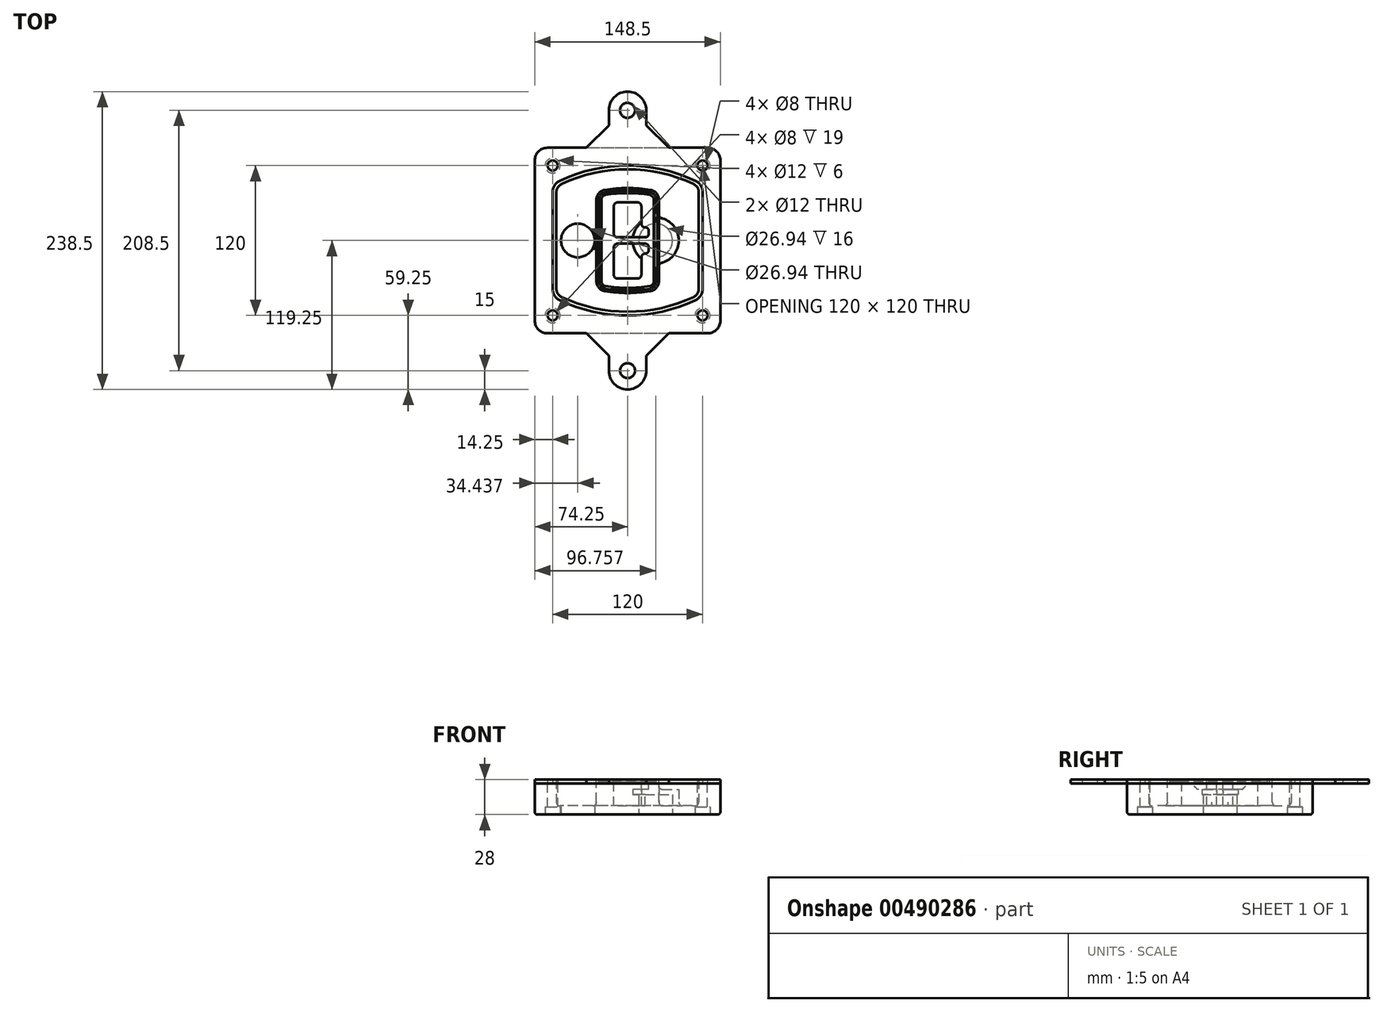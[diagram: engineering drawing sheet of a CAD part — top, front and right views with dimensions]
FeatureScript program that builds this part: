
annotation { "Feature Type Name" : "Feature", "Feature Type Description" : "" }
export const myFeature = defineFeature(function(context is Context, id is Id, definition is map)
    precondition{}
    {
        {
            var Q0;
            Q0=qCreatedBy(makeId("Top.planeOp"),FACE);
            var sketch = newSketch(context, id + "F0", { "sketchPlane" : qUnion([Q0])});
            skPoint(sketch, "E0.rect.middle", {"position": v(0, 0) * mm});
            skLineSegment(sketch, "E1.bottom", {"start": v(-64.25, -74.25) * mm, "end": v(64.25, -74.25) * mm});
            skLineSegment(sketch, "E1.top", {"start": v(-64.25, 74.25) * mm, "end": v(64.25, 74.25) * mm});
            skLineSegment(sketch, "E1.left", {"start": v(-74.25, -64.25) * mm, "end": v(-74.25, 64.25) * mm});
            skLineSegment(sketch, "E1.right", {"start": v(74.25, -64.25) * mm, "end": v(74.25, 64.25) * mm});
            skLineSegment(sketch, "E2", {"start": v(-74.25, 74.25) * mm, "end": v(74.25, -74.25) * mm, "construction": true});
            skLineSegment(sketch, "E3", {"start": v(74.25, 74.25) * mm, "end": v(-74.25, -74.25) * mm, "construction": true});
            skCircle(sketch, "E4", {"center": v(-60, 60) * mm, "radius": 4 * mm});
            skCircle(sketch, "E5", {"center": v(60, 60) * mm, "radius": 4 * mm});
            skCircle(sketch, "E6", {"center": v(60, -60) * mm, "radius": 4 * mm});
            skCircle(sketch, "E7", {"center": v(-60, -60) * mm, "radius": 4 * mm});
            skLineSegment(sketch, "E8", {"start": v(-60, 60) * mm, "end": v(60, 60) * mm, "construction": true});
            skLineSegment(sketch, "E9", {"start": v(60, 60) * mm, "end": v(60, -60) * mm, "construction": true});
            skLineSegment(sketch, "E10", {"start": v(60, -60) * mm, "end": v(-60, -60) * mm, "construction": true});
            skLineSegment(sketch, "E11", {"start": v(-60, -60) * mm, "end": v(-60, 60) * mm, "construction": true});
            skLineSegment(sketch, "E12", {"start": v(-60, 38.83) * mm, "end": v(-60, -38.83) * mm});
            skLineSegment(sketch, "E13", {"start": v(60, 38.83) * mm, "end": v(60, -38.83) * mm});
            skArc(sketch, "E14", {"start": v(54.26, 47.88) * mm, "mid": v(0, 60) * mm, "end": v(-54.26, 47.88) * mm});
            skArc(sketch, "E15", {"start": v(-54.26, -47.88) * mm, "mid": v(0, -60) * mm, "end": v(54.26, -47.88) * mm});
            skLineSegment(sketch, "E16", {"start": v(-60, 0) * mm, "end": v(60, 0) * mm, "construction": true});
            skPoint(sketch, "E17.visualSharp", {"position": v(-60, -45) * mm});
            skArc(sketch, "E17.filletArc", {"start": v(-60, -38.83) * mm, "mid": v(-58.44, -44.2) * mm, "end": v(-54.26, -47.88) * mm});
            skPoint(sketch, "E18.visualSharp", {"position": v(-60, 45) * mm});
            skArc(sketch, "E18.filletArc", {"start": v(-54.26, 47.88) * mm, "mid": v(-58.44, 44.2) * mm, "end": v(-60, 38.83) * mm});
            skPoint(sketch, "E19.visualSharp", {"position": v(60, 45) * mm});
            skArc(sketch, "E19.filletArc", {"start": v(60, 38.83) * mm, "mid": v(58.44, 44.2) * mm, "end": v(54.26, 47.88) * mm});
            skPoint(sketch, "E20.visualSharp", {"position": v(60, -45) * mm});
            skArc(sketch, "E20.filletArc", {"start": v(54.26, -47.88) * mm, "mid": v(58.44, -44.2) * mm, "end": v(60, -38.83) * mm});
            skPoint(sketch, "E21.visualSharp", {"position": v(-74.25, 74.25) * mm});
            skArc(sketch, "E21.filletArc", {"start": v(-64.25, 74.25) * mm, "mid": v(-71.32, 71.32) * mm, "end": v(-74.25, 64.25) * mm});
            skPoint(sketch, "E22.visualSharp", {"position": v(74.25, 74.25) * mm});
            skArc(sketch, "E22.filletArc", {"start": v(74.25, 64.25) * mm, "mid": v(71.32, 71.32) * mm, "end": v(64.25, 74.25) * mm});
            skPoint(sketch, "E23.visualSharp", {"position": v(74.25, -74.25) * mm});
            skArc(sketch, "E23.filletArc", {"start": v(64.25, -74.25) * mm, "mid": v(71.32, -71.32) * mm, "end": v(74.25, -64.25) * mm});
            skPoint(sketch, "E24.visualSharp", {"position": v(-74.25, -74.25) * mm});
            skArc(sketch, "E24.filletArc", {"start": v(-74.25, -64.25) * mm, "mid": v(-71.32, -71.32) * mm, "end": v(-64.25, -74.25) * mm});
            skArc(sketch, "E25.0", {"start": v(57, 38.83) * mm, "mid": v(55.9, 42.58) * mm, "end": v(52.98, 45.17) * mm});
            skLineSegment(sketch, "E25.1", {"start": v(57, 38.83) * mm, "end": v(57, -38.83) * mm});
            skArc(sketch, "E25.2", {"start": v(52.98, -45.17) * mm, "mid": v(55.9, -42.58) * mm, "end": v(57, -38.83) * mm});
            skArc(sketch, "E25.3", {"start": v(-52.98, -45.17) * mm, "mid": v(0, -57) * mm, "end": v(52.98, -45.17) * mm});
            skArc(sketch, "E25.4", {"start": v(-57, -38.83) * mm, "mid": v(-55.9, -42.58) * mm, "end": v(-52.98, -45.17) * mm});
            skArc(sketch, "E25.5", {"start": v(52.98, 45.17) * mm, "mid": v(0, 57) * mm, "end": v(-52.98, 45.17) * mm});
            skLineSegment(sketch, "E25.6", {"start": v(-57, 38.83) * mm, "end": v(-57, -38.83) * mm});
            skArc(sketch, "E25.7", {"start": v(-52.98, 45.17) * mm, "mid": v(-55.9, 42.58) * mm, "end": v(-57, 38.83) * mm});
            skArc(sketch, "E26.0", {"start": v(-55.96, 51.5) * mm, "mid": v(-61.82, 46.33) * mm, "end": v(-64, 38.83) * mm});
            skArc(sketch, "E26.1", {"start": v(55.96, 51.5) * mm, "mid": v(0, 64) * mm, "end": v(-55.96, 51.5) * mm});
            skArc(sketch, "E26.2", {"start": v(64, 38.83) * mm, "mid": v(61.82, 46.33) * mm, "end": v(55.96, 51.5) * mm});
            skLineSegment(sketch, "E26.3", {"start": v(64, 38.83) * mm, "end": v(64, -38.83) * mm});
            skArc(sketch, "E26.4", {"start": v(55.96, -51.5) * mm, "mid": v(61.82, -46.33) * mm, "end": v(64, -38.83) * mm});
            skLineSegment(sketch, "E26.5", {"start": v(-64, 38.83) * mm, "end": v(-64, -38.83) * mm});
            skArc(sketch, "E26.6", {"start": v(-55.96, -51.5) * mm, "mid": v(0, -64) * mm, "end": v(55.96, -51.5) * mm});
            skArc(sketch, "E26.7", {"start": v(-64, -38.83) * mm, "mid": v(-61.82, -46.33) * mm, "end": v(-55.96, -51.5) * mm});
            skSolve(sketch);
        }
        {
            var Q0;
            Q0=makeQuery(id+"F0.imprint","IMPRINT",FACE,{"disambiguationData":[TD([[makeQuery(id+"F0.imprint","IMPRINT",EDGE,{"derivedFrom":sQuery(id+"F0.wireOp",EDGE,"E1.bottom")}),1.0]])]});
            var Q1;
            Q1=makeQuery(id+"F0.imprint","IMPRINT",FACE,{"disambiguationData":[TD([[makeQuery(id+"F0.imprint","IMPRINT",EDGE,{"derivedFrom":sQuery(id+"F0.wireOp",EDGE,"E12")}),1.0]])]});
            var Q2;
            Q2=makeQuery(id+"F0.imprint","IMPRINT",FACE,{"disambiguationData":[TD([[makeQuery(id+"F0.imprint","IMPRINT",EDGE,{"derivedFrom":sQuery(id+"F0.wireOp",EDGE,"E25.0")}),1.0]])]});
            var Q3;
            Q3=makeQuery(id+"F0.imprint","IMPRINT",FACE,{"disambiguationData":[TD([[makeQuery(id+"F0.imprint","IMPRINT",EDGE,{"derivedFrom":sQuery(id+"F0.wireOp",EDGE,"E12")}),-1.0]])]});
            extrude(context, id + "F1", {"entities" : qUnion([Q0, Q1, Q2, Q3]), "oppositeDirection" : true, "depth" : 25 * mm});
        }
        {
            var Q0;
            Q0=makeQuery(id+"F0.imprint","IMPRINT",FACE,{"disambiguationData":[TD([[makeQuery(id+"F0.imprint","IMPRINT",EDGE,{"derivedFrom":sQuery(id+"F0.wireOp",EDGE,"E12")}),1.0]])]});
            extrude(context, id + "F2", {"entities" : qUnion([Q0]), "operationType" : NewBodyOperationType.ADD, "depth" : 3 * mm});
        }
        {
            var Q0;
            Q0=makeQuery(id+"F0.imprint","IMPRINT",FACE,{"disambiguationData":[TD([[makeQuery(id+"F0.imprint","IMPRINT",EDGE,{"derivedFrom":sQuery(id+"F0.wireOp",EDGE,"E25.0")}),1.0]])]});
            extrude(context, id + "F3", {"entities" : qUnion([Q0]), "operationType" : NewBodyOperationType.REMOVE, "oppositeDirection" : true, "depth" : 18 * mm});
        }
        {
            var Q0;
            Q0=makeQuery(id+"F2.opExtrude","CAP_FACE",FACE,{"disambiguationData":[OSD([sQuery(id+"F0.wireOp",EDGE,"E12"),sQuery(id+"F0.wireOp",EDGE,"E13"),sQuery(id+"F0.wireOp",EDGE,"E14"),sQuery(id+"F0.wireOp",EDGE,"E15"),sQuery(id+"F0.wireOp",EDGE,"E17.filletArc"),sQuery(id+"F0.wireOp",EDGE,"E18.filletArc"),sQuery(id+"F0.wireOp",EDGE,"E19.filletArc"),sQuery(id+"F0.wireOp",EDGE,"E20.filletArc"),sQuery(id+"F0.wireOp",EDGE,"E25.0"),sQuery(id+"F0.wireOp",EDGE,"E25.1"),sQuery(id+"F0.wireOp",EDGE,"E25.2"),sQuery(id+"F0.wireOp",EDGE,"E25.3"),sQuery(id+"F0.wireOp",EDGE,"E25.4"),sQuery(id+"F0.wireOp",EDGE,"E25.5"),sQuery(id+"F0.wireOp",EDGE,"E25.6"),sQuery(id+"F0.wireOp",EDGE,"E25.7")])],"isStart":false});
            var sketch = newSketch(context, id + "F4", { "sketchPlane" : qUnion([Q0])});
            skArc(sketch, "E27.0", {"start": v(-18.34, -40.45) * mm, "mid": v(0, -42) * mm, "end": v(18.34, -40.45) * mm});
            skArc(sketch, "E28.0", {"start": v(18.34, 40.45) * mm, "mid": v(0, 42) * mm, "end": v(-18.34, 40.45) * mm});
            skLineSegment(sketch, "E29", {"start": v(-25, 32.57) * mm, "end": v(-25, -32.57) * mm});
            skLineSegment(sketch, "E30", {"start": v(25, 32.57) * mm, "end": v(25, -32.57) * mm});
            skLineSegment(sketch, "E31", {"start": v(-25, 39.1) * mm, "end": v(25, 39.1) * mm, "construction": true});
            skLineSegment(sketch, "E32", {"start": v(-25, -39.1) * mm, "end": v(25, -39.1) * mm, "construction": true});
            skPoint(sketch, "E33.visualSharp", {"position": v(-25, 39.1) * mm});
            skArc(sketch, "E33.filletArc", {"start": v(-18.34, 40.45) * mm, "mid": v(-23.11, 37.73) * mm, "end": v(-25, 32.57) * mm});
            skPoint(sketch, "E34.visualSharp", {"position": v(25, 39.1) * mm});
            skArc(sketch, "E34.filletArc", {"start": v(25, 32.57) * mm, "mid": v(23.11, 37.73) * mm, "end": v(18.34, 40.45) * mm});
            skPoint(sketch, "E35.visualSharp", {"position": v(25, -39.1) * mm});
            skArc(sketch, "E35.filletArc", {"start": v(18.34, -40.45) * mm, "mid": v(23.11, -37.73) * mm, "end": v(25, -32.57) * mm});
            skPoint(sketch, "E36.visualSharp", {"position": v(-25, -39.1) * mm});
            skArc(sketch, "E36.filletArc", {"start": v(-25, -32.57) * mm, "mid": v(-23.11, -37.73) * mm, "end": v(-18.34, -40.45) * mm});
            skArc(sketch, "E37.0", {"start": v(52.98, 45.17) * mm, "mid": v(0, 57) * mm, "end": v(-52.98, 45.17) * mm});
            skArc(sketch, "E37.1", {"start": v(-52.98, 45.17) * mm, "mid": v(-55.9, 42.58) * mm, "end": v(-57, 38.83) * mm});
            skLineSegment(sketch, "E37.2", {"start": v(-57, 38.83) * mm, "end": v(-57, -38.83) * mm});
            skArc(sketch, "E37.3", {"start": v(-57, -38.83) * mm, "mid": v(-55.9, -42.58) * mm, "end": v(-52.98, -45.17) * mm});
            skArc(sketch, "E37.4", {"start": v(-52.98, -45.17) * mm, "mid": v(0, -57) * mm, "end": v(52.98, -45.17) * mm});
            skArc(sketch, "E37.5", {"start": v(52.98, -45.17) * mm, "mid": v(55.9, -42.58) * mm, "end": v(57, -38.83) * mm});
            skLineSegment(sketch, "E37.6", {"start": v(57, 38.83) * mm, "end": v(57, -38.83) * mm});
            skArc(sketch, "E37.7", {"start": v(57, 38.83) * mm, "mid": v(55.9, 42.58) * mm, "end": v(52.98, 45.17) * mm});
            skLineSegment(sketch, "E38.0", {"start": v(23, 32.57) * mm, "end": v(23, -32.57) * mm});
            skArc(sketch, "E38.1", {"start": v(18, -38.48) * mm, "mid": v(21.58, -36.44) * mm, "end": v(23, -32.57) * mm});
            skArc(sketch, "E38.2", {"start": v(-18, -38.48) * mm, "mid": v(0, -40) * mm, "end": v(18, -38.48) * mm});
            skArc(sketch, "E38.3", {"start": v(-23, -32.57) * mm, "mid": v(-21.58, -36.44) * mm, "end": v(-18, -38.48) * mm});
            skLineSegment(sketch, "E38.4", {"start": v(-23, 32.57) * mm, "end": v(-23, -32.57) * mm});
            skArc(sketch, "E38.5", {"start": v(23, 32.57) * mm, "mid": v(21.58, 36.44) * mm, "end": v(18, 38.48) * mm});
            skArc(sketch, "E38.6", {"start": v(-18, 38.48) * mm, "mid": v(-21.58, 36.44) * mm, "end": v(-23, 32.57) * mm});
            skArc(sketch, "E38.7", {"start": v(18, 38.48) * mm, "mid": v(0, 40) * mm, "end": v(-18, 38.48) * mm});
            skArc(sketch, "E39.0", {"start": v(21, 32.57) * mm, "mid": v(20.06, 35.15) * mm, "end": v(17.67, 36.5) * mm});
            skLineSegment(sketch, "E39.1", {"start": v(21, 32.57) * mm, "end": v(21, -32.57) * mm});
            skArc(sketch, "E39.2", {"start": v(17.67, -36.5) * mm, "mid": v(20.06, -35.15) * mm, "end": v(21, -32.57) * mm});
            skArc(sketch, "E39.3", {"start": v(-17.67, -36.5) * mm, "mid": v(0, -38) * mm, "end": v(17.67, -36.5) * mm});
            skArc(sketch, "E39.4", {"start": v(-21, -32.57) * mm, "mid": v(-20.06, -35.15) * mm, "end": v(-17.67, -36.5) * mm});
            skArc(sketch, "E39.5", {"start": v(17.67, 36.5) * mm, "mid": v(0, 38) * mm, "end": v(-17.67, 36.5) * mm});
            skLineSegment(sketch, "E39.6", {"start": v(-21, 32.57) * mm, "end": v(-21, -32.57) * mm});
            skArc(sketch, "E39.7", {"start": v(-17.67, 36.5) * mm, "mid": v(-20.06, 35.15) * mm, "end": v(-21, 32.57) * mm});
            skLineSegment(sketch, "E40", {"start": v(-25, 0) * mm, "end": v(25, 0) * mm, "construction": true});
            skLineSegment(sketch, "E41", {"start": v(-11, 5.5) * mm, "end": v(-11, 27.5) * mm});
            skLineSegment(sketch, "E42", {"start": v(-8, 30.5) * mm, "end": v(8, 30.5) * mm});
            skLineSegment(sketch, "E43", {"start": v(11, 27.5) * mm, "end": v(11, 13.5) * mm});
            skLineSegment(sketch, "E44", {"start": v(14, 10.5) * mm, "end": v(14, 10.5) * mm});
            skLineSegment(sketch, "E45", {"start": v(17, 7.5) * mm, "end": v(17, 5.5) * mm});
            skLineSegment(sketch, "E46", {"start": v(14, 2.5) * mm, "end": v(-8, 2.5) * mm});
            skPoint(sketch, "E47.visualSharp", {"position": v(-11, 30.5) * mm});
            skArc(sketch, "E47.filletArc", {"start": v(-8, 30.5) * mm, "mid": v(-10.12, 29.62) * mm, "end": v(-11, 27.5) * mm});
            skPoint(sketch, "E48.visualSharp", {"position": v(11, 30.5) * mm});
            skArc(sketch, "E48.filletArc", {"start": v(11, 27.5) * mm, "mid": v(10.12, 29.62) * mm, "end": v(8, 30.5) * mm});
            skPoint(sketch, "E49.visualSharp", {"position": v(11, 10.5) * mm});
            skArc(sketch, "E49.filletArc", {"start": v(11, 13.5) * mm, "mid": v(11.88, 11.38) * mm, "end": v(14, 10.5) * mm});
            skPoint(sketch, "E50.visualSharp", {"position": v(17, 10.5) * mm});
            skArc(sketch, "E50.filletArc", {"start": v(17, 7.5) * mm, "mid": v(16.12, 9.62) * mm, "end": v(14, 10.5) * mm});
            skPoint(sketch, "E51.visualSharp", {"position": v(17, 2.5) * mm});
            skArc(sketch, "E51.filletArc", {"start": v(14, 2.5) * mm, "mid": v(16.12, 3.38) * mm, "end": v(17, 5.5) * mm});
            skPoint(sketch, "E52.visualSharp", {"position": v(-11, 2.5) * mm});
            skArc(sketch, "E52.filletArc", {"start": v(-11, 5.5) * mm, "mid": v(-10.12, 3.38) * mm, "end": v(-8, 2.5) * mm});
            skLineSegment(sketch, "E53.0.MirrorCS", {"start": v(14, -2.5) * mm, "end": v(-8, -2.5) * mm});
            skArc(sketch, "E54.0.MirrorCS", {"start": v(-11, -5.5) * mm, "mid": v(-10.12, -3.38) * mm, "end": v(-8, -2.5) * mm});
            skLineSegment(sketch, "E55.0.MirrorCS", {"start": v(-11, -5.5) * mm, "end": v(-11, -27.5) * mm});
            skArc(sketch, "E56.0.MirrorCS", {"start": v(-8, -30.5) * mm, "mid": v(-10.12, -29.62) * mm, "end": v(-11, -27.5) * mm});
            skLineSegment(sketch, "E57.0.MirrorCS", {"start": v(-8, -30.5) * mm, "end": v(8, -30.5) * mm});
            skArc(sketch, "E58.0.MirrorCS", {"start": v(11, -27.5) * mm, "mid": v(10.12, -29.62) * mm, "end": v(8, -30.5) * mm});
            skLineSegment(sketch, "E59.0.MirrorCS", {"start": v(11, -27.5) * mm, "end": v(11, -13.5) * mm});
            skArc(sketch, "E60.0.MirrorCS", {"start": v(11, -13.5) * mm, "mid": v(11.88, -11.38) * mm, "end": v(14, -10.5) * mm});
            skArc(sketch, "E61.0.MirrorCS", {"start": v(17, -7.5) * mm, "mid": v(16.12, -9.62) * mm, "end": v(14, -10.5) * mm});
            skLineSegment(sketch, "E62.0.MirrorCS", {"start": v(17, -7.5) * mm, "end": v(17, -5.5) * mm});
            skArc(sketch, "E63.0.MirrorCS", {"start": v(14, -2.5) * mm, "mid": v(16.12, -3.38) * mm, "end": v(17, -5.5) * mm});
            skSolve(sketch);
        }
        {
            var Q0;
            Q0=makeQuery(id+"F4.imprint","IMPRINT",FACE,{"disambiguationData":[TD([[makeQuery(id+"F4.imprint","IMPRINT",EDGE,{"derivedFrom":sQuery(id+"F4.wireOp",EDGE,"E27.0")}),1.0]])]});
            var Q1;
            Q1=makeQuery(id+"F4.imprint","IMPRINT",FACE,{"disambiguationData":[TD([[makeQuery(id+"F4.imprint","IMPRINT",EDGE,{"derivedFrom":sQuery(id+"F4.wireOp",EDGE,"E38.0")}),-1.0]])]});
            var Q2;
            Q2=makeQuery(id+"F4.imprint","IMPRINT",FACE,{"disambiguationData":[TD([[makeQuery(id+"F4.imprint","IMPRINT",EDGE,{"derivedFrom":sQuery(id+"F4.wireOp",EDGE,"E39.0")}),1.0]])]});
            extrude(context, id + "F5", {"entities" : qUnion([Q0, Q1, Q2]), "operationType" : NewBodyOperationType.ADD, "endBound" : BoundingType.UP_TO_NEXT, "oppositeDirection" : true, "depth" : 25 * mm});
        }
        {
            var Q0;
            Q0=makeQuery(id+"F4.imprint","IMPRINT",FACE,{"disambiguationData":[TD([[makeQuery(id+"F4.imprint","IMPRINT",EDGE,{"derivedFrom":sQuery(id+"F4.wireOp",EDGE,"E38.0")}),-1.0]])]});
            extrude(context, id + "F6", {"entities" : qUnion([Q0]), "operationType" : NewBodyOperationType.REMOVE, "oppositeDirection" : true, "depth" : 2 * mm});
        }
        {
            var Q0;
            Q0=makeQuery(id+"F1.opExtrude","CAP_FACE",FACE,{"disambiguationData":[OSD([sQuery(id+"F0.wireOp",EDGE,"E1.bottom"),sQuery(id+"F0.wireOp",EDGE,"E1.top"),sQuery(id+"F0.wireOp",EDGE,"E1.left"),sQuery(id+"F0.wireOp",EDGE,"E1.right"),sQuery(id+"F0.wireOp",EDGE,"E4"),sQuery(id+"F0.wireOp",EDGE,"E5"),sQuery(id+"F0.wireOp",EDGE,"E6"),sQuery(id+"F0.wireOp",EDGE,"E7"),sQuery(id+"F0.wireOp",EDGE,"E21.filletArc"),sQuery(id+"F0.wireOp",EDGE,"E22.filletArc"),sQuery(id+"F0.wireOp",EDGE,"E23.filletArc"),sQuery(id+"F0.wireOp",EDGE,"E24.filletArc")])],"isStart":false});
            var sketch = newSketch(context, id + "F7", { "sketchPlane" : qUnion([Q0])});
            skCircle(sketch, "E64", {"center": v(22.5, 0) * mm, "radius": 13.47 * mm});
            skCircle(sketch, "E65", {"center": v(-39.81, 0) * mm, "radius": 13.47 * mm});
            skLineSegment(sketch, "E66", {"start": v(74.25, 0) * mm, "end": v(-74.25, 0) * mm});
            skCircle(sketch, "E67", {"center": v(22.5, 0) * mm, "radius": 18.47 * mm});
            skCircle(sketch, "E68", {"center": v(60, -60) * mm, "radius": 6 * mm});
            skCircle(sketch, "E69", {"center": v(-60, -60) * mm, "radius": 6 * mm});
            skCircle(sketch, "E70", {"center": v(-60, 60) * mm, "radius": 6 * mm});
            skCircle(sketch, "E71", {"center": v(60, 60) * mm, "radius": 6 * mm});
            skSolve(sketch);
        }
        {
            var Q0;
            {var subQ1=sQuery(id+"F7.wireOp",EDGE,"E66");var subQ4=sQuery(id+"F7.wireOp",EDGE,"E64");var subQ6=makeQuery(id+"F7.imprint","INTERSECT",VERTEX,{"disambiguationData":[OD(0.0)],"derivedFrom":[subQ4,subQ1]});Q0=makeQuery(id+"F7.imprint","IMPRINT",FACE,{"disambiguationData":[TD([[makeQuery(id+"F7.imprint","IMPRINT",EDGE,{"disambiguationData":[TD([[subQ6,-1.0]])],"derivedFrom":subQ4}),-1.0]])]});}
            var Q1;
            {var subQ0=sQuery(id+"F7.wireOp",EDGE,"E66");var subQ1=sQuery(id+"F7.wireOp",EDGE,"E64");var subQ3=makeQuery(id+"F7.imprint","INTERSECT",VERTEX,{"disambiguationData":[OD(0.0)],"derivedFrom":[subQ1,subQ0]});Q1=makeQuery(id+"F7.imprint","IMPRINT",FACE,{"disambiguationData":[TD([[makeQuery(id+"F7.imprint","IMPRINT",EDGE,{"disambiguationData":[TD([[subQ3,-1.0]])],"derivedFrom":subQ1}),1.0]])]});}
            var Q2;
            {var subQ0=sQuery(id+"F7.wireOp",EDGE,"E66");var subQ1=sQuery(id+"F7.wireOp",EDGE,"E64");var subQ3=makeQuery(id+"F7.imprint","INTERSECT",VERTEX,{"disambiguationData":[OD(0.0)],"derivedFrom":[subQ1,subQ0]});Q2=makeQuery(id+"F7.imprint","IMPRINT",FACE,{"disambiguationData":[TD([[makeQuery(id+"F7.imprint","IMPRINT",EDGE,{"disambiguationData":[TD([[subQ3,1.0]])],"derivedFrom":subQ1}),1.0]])]});}
            var Q3;
            {var subQ1=sQuery(id+"F7.wireOp",EDGE,"E66");var subQ4=sQuery(id+"F7.wireOp",EDGE,"E64");var subQ6=makeQuery(id+"F7.imprint","INTERSECT",VERTEX,{"disambiguationData":[OD(0.0)],"derivedFrom":[subQ4,subQ1]});Q3=makeQuery(id+"F7.imprint","IMPRINT",FACE,{"disambiguationData":[TD([[makeQuery(id+"F7.imprint","IMPRINT",EDGE,{"disambiguationData":[TD([[subQ6,1.0]])],"derivedFrom":subQ4}),-1.0]])]});}
            extrude(context, id + "F8", {"entities" : qUnion([Q0, Q1, Q2, Q3]), "operationType" : NewBodyOperationType.ADD, "oppositeDirection" : true, "depth" : 20 * mm});
        }
        {
            var Q0;
            {var subQ0=sQuery(id+"F7.wireOp",EDGE,"E66");var subQ1=sQuery(id+"F7.wireOp",EDGE,"E64");var subQ3=makeQuery(id+"F7.imprint","INTERSECT",VERTEX,{"disambiguationData":[OD(0.0)],"derivedFrom":[subQ1,subQ0]});Q0=makeQuery(id+"F7.imprint","IMPRINT",FACE,{"disambiguationData":[TD([[makeQuery(id+"F7.imprint","IMPRINT",EDGE,{"disambiguationData":[TD([[subQ3,-1.0]])],"derivedFrom":subQ1}),1.0]])]});}
            var Q1;
            {var subQ0=sQuery(id+"F7.wireOp",EDGE,"E66");var subQ1=sQuery(id+"F7.wireOp",EDGE,"E64");var subQ3=makeQuery(id+"F7.imprint","INTERSECT",VERTEX,{"disambiguationData":[OD(0.0)],"derivedFrom":[subQ1,subQ0]});Q1=makeQuery(id+"F7.imprint","IMPRINT",FACE,{"disambiguationData":[TD([[makeQuery(id+"F7.imprint","IMPRINT",EDGE,{"disambiguationData":[TD([[subQ3,1.0]])],"derivedFrom":subQ1}),1.0]])]});}
            extrude(context, id + "F9", {"entities" : qUnion([Q0, Q1]), "operationType" : NewBodyOperationType.REMOVE, "oppositeDirection" : true, "depth" : 16 * mm});
        }
        {
            var Q0;
            {var subQ0=sQuery(id+"F7.wireOp",EDGE,"E66");var subQ1=sQuery(id+"F7.wireOp",EDGE,"E65");var subQ3=makeQuery(id+"F7.imprint","INTERSECT",VERTEX,{"disambiguationData":[OD(0.0)],"derivedFrom":[subQ1,subQ0]});Q0=makeQuery(id+"F7.imprint","IMPRINT",FACE,{"disambiguationData":[TD([[makeQuery(id+"F7.imprint","IMPRINT",EDGE,{"disambiguationData":[TD([[subQ3,-1.0]])],"derivedFrom":subQ1}),1.0]])]});}
            var Q1;
            {var subQ0=sQuery(id+"F7.wireOp",EDGE,"E66");var subQ1=sQuery(id+"F7.wireOp",EDGE,"E65");var subQ3=makeQuery(id+"F7.imprint","INTERSECT",VERTEX,{"disambiguationData":[OD(0.0)],"derivedFrom":[subQ1,subQ0]});Q1=makeQuery(id+"F7.imprint","IMPRINT",FACE,{"disambiguationData":[TD([[makeQuery(id+"F7.imprint","IMPRINT",EDGE,{"disambiguationData":[TD([[subQ3,1.0]])],"derivedFrom":subQ1}),1.0]])]});}
            extrude(context, id + "F10", {"entities" : qUnion([Q0, Q1]), "operationType" : NewBodyOperationType.REMOVE, "oppositeDirection" : true, "depth" : 25 * mm});
        }
        {
            var Q0;
            Q0=makeQuery(id+"F7.imprint","IMPRINT",FACE,{"disambiguationData":[TD([[makeQuery(id+"F7.imprint","IMPRINT",EDGE,{"derivedFrom":sQuery(id+"F7.wireOp",EDGE,"E68")}),1.0]])]});
            var Q1;
            Q1=makeQuery(id+"F7.imprint","IMPRINT",FACE,{"disambiguationData":[TD([[makeQuery(id+"F7.imprint","IMPRINT",EDGE,{"derivedFrom":makeQuery(id+"F1.opExtrude","CAP_EDGE",EDGE,{"disambiguationData":[OSD([sQuery(id+"F0.wireOp",EDGE,"E5")])],"isStart":false})}),-1.0]])]});
            var Q2;
            Q2=makeQuery(id+"F7.imprint","IMPRINT",FACE,{"disambiguationData":[TD([[makeQuery(id+"F7.imprint","IMPRINT",EDGE,{"derivedFrom":sQuery(id+"F7.wireOp",EDGE,"E69")}),1.0]])]});
            var Q3;
            Q3=makeQuery(id+"F7.imprint","IMPRINT",FACE,{"disambiguationData":[TD([[makeQuery(id+"F7.imprint","IMPRINT",EDGE,{"derivedFrom":makeQuery(id+"F1.opExtrude","CAP_EDGE",EDGE,{"disambiguationData":[OSD([sQuery(id+"F0.wireOp",EDGE,"E4")])],"isStart":false})}),-1.0]])]});
            var Q4;
            Q4=makeQuery(id+"F7.imprint","IMPRINT",FACE,{"disambiguationData":[TD([[makeQuery(id+"F7.imprint","IMPRINT",EDGE,{"derivedFrom":sQuery(id+"F7.wireOp",EDGE,"E70")}),1.0]])]});
            var Q5;
            Q5=makeQuery(id+"F7.imprint","IMPRINT",FACE,{"disambiguationData":[TD([[makeQuery(id+"F7.imprint","IMPRINT",EDGE,{"derivedFrom":makeQuery(id+"F1.opExtrude","CAP_EDGE",EDGE,{"disambiguationData":[OSD([sQuery(id+"F0.wireOp",EDGE,"E7")])],"isStart":false})}),-1.0]])]});
            var Q6;
            Q6=makeQuery(id+"F7.imprint","IMPRINT",FACE,{"disambiguationData":[TD([[makeQuery(id+"F7.imprint","IMPRINT",EDGE,{"derivedFrom":sQuery(id+"F7.wireOp",EDGE,"E71")}),1.0]])]});
            var Q7;
            Q7=makeQuery(id+"F7.imprint","IMPRINT",FACE,{"disambiguationData":[TD([[makeQuery(id+"F7.imprint","IMPRINT",EDGE,{"derivedFrom":makeQuery(id+"F1.opExtrude","CAP_EDGE",EDGE,{"disambiguationData":[OSD([sQuery(id+"F0.wireOp",EDGE,"E6")])],"isStart":false})}),-1.0]])]});
            extrude(context, id + "F11", {"entities" : qUnion([Q0, Q1, Q2, Q3, Q4, Q5, Q6, Q7]), "operationType" : NewBodyOperationType.REMOVE, "oppositeDirection" : true, "depth" : 6 * mm});
        }
        {
            var Q0;
            Q0=makeQuery(id+"F9.boolean.opBoolean","COPY",FACE,{"derivedFrom":makeQuery(id+"F9.opExtrude","CAP_FACE",FACE,{"disambiguationData":[OSD([sQuery(id+"F7.wireOp",EDGE,"E64")])],"isStart":false})});
            var sketch = newSketch(context, id + "F12", { "sketchPlane" : qUnion([Q0])});
            skArc(sketch, "E72.0", {"start": v(11, 14.45) * mm, "mid": v(6.45, 9.13) * mm, "end": v(4.2, 2.5) * mm});
            skArc(sketch, "E72.1", {"start": v(4.2, -2.5) * mm, "mid": v(6.45, -9.13) * mm, "end": v(11, -14.45) * mm});
            skLineSegment(sketch, "E73", {"start": v(4.2, -2.5) * mm, "end": v(14, -2.5) * mm});
            skLineSegment(sketch, "E74.0", {"start": v(14, 2.5) * mm, "end": v(4.2, 2.5) * mm});
            skArc(sketch, "E74.1", {"start": v(14, 2.5) * mm, "mid": v(16.12, 3.38) * mm, "end": v(17, 5.5) * mm});
            skLineSegment(sketch, "E74.2", {"start": v(17, 7.5) * mm, "end": v(17, 5.5) * mm});
            skArc(sketch, "E74.3", {"start": v(17, 7.5) * mm, "mid": v(16.12, 9.62) * mm, "end": v(14, 10.5) * mm});
            skArc(sketch, "E74.4", {"start": v(11, 13.5) * mm, "mid": v(11.88, 11.38) * mm, "end": v(14, 10.5) * mm});
            skLineSegment(sketch, "E74.5", {"start": v(11, 14.45) * mm, "end": v(11, 13.5) * mm});
            skLineSegment(sketch, "E74.7", {"start": v(14, -2.5) * mm, "end": v(4.2, -2.5) * mm});
            skArc(sketch, "E74.8", {"start": v(14, -2.5) * mm, "mid": v(16.12, -3.38) * mm, "end": v(17, -5.5) * mm});
            skLineSegment(sketch, "E74.9", {"start": v(17, -7.5) * mm, "end": v(17, -5.5) * mm});
            skArc(sketch, "E74.10", {"start": v(17, -7.5) * mm, "mid": v(16.12, -9.62) * mm, "end": v(14, -10.5) * mm});
            skArc(sketch, "E74.11", {"start": v(11, -13.5) * mm, "mid": v(11.88, -11.38) * mm, "end": v(14, -10.5) * mm});
            skLineSegment(sketch, "E74.12", {"start": v(11, -14.45) * mm, "end": v(11, -13.5) * mm});
            skPoint(sketch, "E75.orphan", {"position": v(11, -27.5) * mm});
            skPoint(sketch, "E76.orphan", {"position": v(-8, -2.5) * mm});
            skPoint(sketch, "E77.orphan", {"position": v(-8, 2.5) * mm});
            skPoint(sketch, "E78.orphan", {"position": v(11, 27.5) * mm});
            skSolve(sketch);
        }
        {
            var Q0;
            {var subQ7=sQuery(id+"F12.wireOp",EDGE,"E72.0");var subQ14=sQuery(id+"F12.wireOp",EDGE,"E72.1");var subQ16=sQuery(id+"F12.wireOp",EDGE,"E74.1");var subQ18=sQuery(id+"F12.wireOp",EDGE,"E74.8");Q0=qUnion([makeQuery(id+"F12.imprint","IMPRINT",FACE,{"disambiguationData":[TD([[makeQuery(id+"F12.imprint","IMPRINT",EDGE,{"derivedFrom":subQ7}),1.0]])]}),makeQuery(id+"F12.imprint","IMPRINT",FACE,{"disambiguationData":[TD([[makeQuery(id+"F12.imprint","IMPRINT",EDGE,{"derivedFrom":subQ14}),1.0]])]}),makeQuery(id+"F12.imprint","IMPRINT",FACE,{"disambiguationData":[TD([[makeQuery(id+"F12.imprint","IMPRINT",EDGE,{"derivedFrom":subQ16}),1.0]])]}),makeQuery(id+"F12.imprint","IMPRINT",FACE,{"disambiguationData":[TD([[makeQuery(id+"F12.imprint","IMPRINT",EDGE,{"derivedFrom":subQ18}),-1.0]])]})]);}
            var Q1;
            Q1=makeQuery(id+"F5.boolean.opBoolean","SPLIT",FACE,{"disambiguationData":[TD([makeQuery(id+"F5.opExtrude","SWEPT_FACE",FACE,{"disambiguationData":[OSD([sQuery(id+"F4.wireOp",EDGE,"E41")])]})])],"derivedFrom":makeQuery(id+"F3.boolean.opBoolean","COPY",FACE,{"derivedFrom":makeQuery(id+"F3.opExtrude","CAP_FACE",FACE,{"disambiguationData":[OSD([sQuery(id+"F0.wireOp",EDGE,"E25.0"),sQuery(id+"F0.wireOp",EDGE,"E25.1"),sQuery(id+"F0.wireOp",EDGE,"E25.2"),sQuery(id+"F0.wireOp",EDGE,"E25.3"),sQuery(id+"F0.wireOp",EDGE,"E25.4"),sQuery(id+"F0.wireOp",EDGE,"E25.5"),sQuery(id+"F0.wireOp",EDGE,"E25.6"),sQuery(id+"F0.wireOp",EDGE,"E25.7")])],"isStart":false})})});
            extrude(context, id + "F13", {"entities" : qUnion([Q0]), "operationType" : NewBodyOperationType.REMOVE, "endBound" : BoundingType.UP_TO_SURFACE, "endBoundEntityFace" : qUnion([Q1]), "depth" : 25 * mm});
        }
        {
            var Q0;
            Q0=makeQuery(id+"F3.boolean.opBoolean","COPY",EDGE,{"derivedFrom":makeQuery(id+"F3.opExtrude","CAP_EDGE",EDGE,{"disambiguationData":[OSD([sQuery(id+"F0.wireOp",EDGE,"E25.6")])],"isStart":false})});
            var Q1;
            Q1=makeQuery(id+"F8.boolean.opBoolean","INTERSECT",EDGE,{"derivedFrom":[makeQuery(id+"F5.opExtrude","SWEPT_FACE",FACE,{"disambiguationData":[OSD([sQuery(id+"F4.wireOp",EDGE,"E30")])]}),makeQuery(id+"F8.opExtrude","CAP_FACE",FACE,{"disambiguationData":[OSD([sQuery(id+"F7.wireOp",EDGE,"E67")])],"isStart":false})]});
            var Q2;
            Q2=makeQuery(id+"F8.boolean.opBoolean","INTERSECT",EDGE,{"disambiguationData":[OD(1.0)],"derivedFrom":[makeQuery(id+"F5.opExtrude","SWEPT_FACE",FACE,{"disambiguationData":[OSD([sQuery(id+"F4.wireOp",EDGE,"E30")])]}),makeQuery(id+"F8.opExtrude","SWEPT_FACE",FACE,{"disambiguationData":[OSD([sQuery(id+"F7.wireOp",EDGE,"E67")])]})]});
            var Q3;
            {var subQ0=sQuery(id+"F4.wireOp",EDGE,"E30");Q3=makeQuery(id+"F8.boolean.opBoolean","SPLIT",EDGE,{"disambiguationData":[TD([makeQuery(id+"F5.opExtrude","SWEPT_FACE",FACE,{"disambiguationData":[OSD([sQuery(id+"F4.wireOp",EDGE,"E35.filletArc")])]})])],"derivedFrom":makeQuery(id+"F5.opExtrude","CAP_EDGE",EDGE,{"disambiguationData":[OSD([subQ0])],"isStart":false})});}
            var Q4;
            {var subQ0=sQuery(id+"F0.wireOp",EDGE,"E25.7");var subQ1=sQuery(id+"F0.wireOp",EDGE,"E25.1");var subQ2=sQuery(id+"F0.wireOp",EDGE,"E25.6");var subQ3=sQuery(id+"F0.wireOp",EDGE,"E25.5");var subQ4=sQuery(id+"F0.wireOp",EDGE,"E25.4");var subQ5=sQuery(id+"F0.wireOp",EDGE,"E25.0");var subQ6=sQuery(id+"F0.wireOp",EDGE,"E25.2");var subQ7=sQuery(id+"F0.wireOp",EDGE,"E25.3");Q4=makeQuery(id+"F8.boolean.opBoolean","INTERSECT",EDGE,{"derivedFrom":[makeQuery(id+"F5.boolean.opBoolean","SPLIT",FACE,{"disambiguationData":[TD([makeQuery(id+"F2.opExtrude","SWEPT_FACE",FACE,{"disambiguationData":[OSD([subQ5])]})])],"derivedFrom":makeQuery(id+"F3.boolean.opBoolean","COPY",FACE,{"derivedFrom":makeQuery(id+"F3.opExtrude","CAP_FACE",FACE,{"disambiguationData":[OSD([subQ5,subQ1,subQ6,subQ7,subQ4,subQ3,subQ2,subQ0])],"isStart":false})})}),makeQuery(id+"F8.opExtrude","SWEPT_FACE",FACE,{"disambiguationData":[OSD([sQuery(id+"F7.wireOp",EDGE,"E67")])]})]});}
            var Q5;
            Q5=makeQuery(id+"F8.boolean.opBoolean","INTERSECT",EDGE,{"disambiguationData":[OD(0.0)],"derivedFrom":[makeQuery(id+"F5.opExtrude","SWEPT_FACE",FACE,{"disambiguationData":[OSD([sQuery(id+"F4.wireOp",EDGE,"E30")])]}),makeQuery(id+"F8.opExtrude","SWEPT_FACE",FACE,{"disambiguationData":[OSD([sQuery(id+"F7.wireOp",EDGE,"E67")])]})]});
            fillet(context, id + "F14", {"entities" : qUnion([Q0, Q1, Q2, Q3, Q4, Q5]), "radius" : 3 * mm, "tangentPropagation" : true, "allowEdgeOverflow" : false});
        }
        {
            var Q0;
            Q0=makeQuery(id+"F1.opExtrude","CAP_EDGE",EDGE,{"disambiguationData":[OSD([sQuery(id+"F0.wireOp",EDGE,"E1.bottom")])],"isStart":false});
            fillet(context, id + "F15", {"entities" : qUnion([Q0]), "radius" : 2 * mm, "tangentPropagation" : true, "allowEdgeOverflow" : false});
        }
        {
            var Q0;
            {var subQ0=sQuery(id+"F0.wireOp",EDGE,"E21.filletArc");var subQ1=sQuery(id+"F0.wireOp",EDGE,"E7");var subQ2=sQuery(id+"F0.wireOp",EDGE,"E6");var subQ3=sQuery(id+"F0.wireOp",EDGE,"E5");var subQ4=sQuery(id+"F0.wireOp",EDGE,"E4");var subQ5=sQuery(id+"F0.wireOp",EDGE,"E22.filletArc");var subQ6=sQuery(id+"F0.wireOp",EDGE,"E1.bottom");var subQ7=sQuery(id+"F0.wireOp",EDGE,"E1.right");var subQ8=sQuery(id+"F0.wireOp",EDGE,"E1.top");var subQ9=sQuery(id+"F0.wireOp",EDGE,"E1.left");var subQ10=sQuery(id+"F0.wireOp",EDGE,"E23.filletArc");var subQ11=sQuery(id+"F0.wireOp",EDGE,"E24.filletArc");Q0=makeQuery(id+"F2.boolean.opBoolean","SPLIT",FACE,{"disambiguationData":[TD([makeQuery(id+"F1.opExtrude","SWEPT_FACE",FACE,{"disambiguationData":[OSD([subQ6])]})])],"derivedFrom":makeQuery(id+"F1.opExtrude","CAP_FACE",FACE,{"disambiguationData":[OSD([subQ6,subQ8,subQ9,subQ7,subQ4,subQ3,subQ2,subQ1,subQ0,subQ5,subQ10,subQ11])],"isStart":true})});}
            var sketch = newSketch(context, id + "F16", { "sketchPlane" : qUnion([Q0])});
            skLineSegment(sketch, "E79", {"start": v(0, 74.25) * mm, "end": v(0, 104.25) * mm, "construction": true});
            skArc(sketch, "E80", {"start": v(15, 104.25) * mm, "mid": v(0, 119.25) * mm, "end": v(-15, 104.25) * mm});
            skLineSegment(sketch, "E81", {"start": v(15, 104.25) * mm, "end": v(15, 92.25) * mm});
            skLineSegment(sketch, "E82", {"start": v(-15, 104.25) * mm, "end": v(-15, 92.25) * mm});
            skLineSegment(sketch, "E83", {"start": v(-15, 92.25) * mm, "end": v(-33, 74.25) * mm});
            skLineSegment(sketch, "E84", {"start": v(15, 92.25) * mm, "end": v(33, 74.25) * mm});
            skCircle(sketch, "E85", {"center": v(0, 104.25) * mm, "radius": 6 * mm});
            skLineSegment(sketch, "E86", {"start": v(-74.25, 0) * mm, "end": v(74.25, 0) * mm, "construction": true});
            skLineSegment(sketch, "E87.MirrorCS", {"start": v(15, -104.25) * mm, "end": v(15, -92.25) * mm});
            skArc(sketch, "E88.MirrorCS", {"start": v(15, -104.25) * mm, "mid": v(0, -119.25) * mm, "end": v(-15, -104.25) * mm});
            skLineSegment(sketch, "E89.MirrorCS", {"start": v(0, -74.25) * mm, "end": v(0, -104.25) * mm, "construction": true});
            skLineSegment(sketch, "E90.MirrorCS", {"start": v(-15, -104.25) * mm, "end": v(-15, -92.25) * mm});
            skLineSegment(sketch, "E91.MirrorCS", {"start": v(-15, -92.25) * mm, "end": v(-33, -74.25) * mm});
            skLineSegment(sketch, "E92.MirrorCS", {"start": v(15, -92.25) * mm, "end": v(33, -74.25) * mm});
            skCircle(sketch, "E93.MirrorC", {"center": v(0, -104.25) * mm, "radius": 6 * mm});
            skSolve(sketch);
        }
        {
            var Q0;
            Q0=makeQuery(id+"F16.imprint","IMPRINT",FACE,{"disambiguationData":[TD([[makeQuery(id+"F16.imprint","IMPRINT",EDGE,{"derivedFrom":sQuery(id+"F16.wireOp",EDGE,"E80")}),1.0]])]});
            var Q1;
            Q1=makeQuery(id+"F16.imprint","IMPRINT",FACE,{"disambiguationData":[TD([[makeQuery(id+"F16.imprint","IMPRINT",EDGE,{"derivedFrom":makeQuery(id+"F1.opExtrude","CAP_EDGE",EDGE,{"disambiguationData":[OSD([sQuery(id+"F0.wireOp",EDGE,"E1.left")])],"isStart":true})}),-1.0]])]});
            var Q2;
            Q2=makeQuery(id+"F16.imprint","IMPRINT",FACE,{"disambiguationData":[TD([[makeQuery(id+"F16.imprint","IMPRINT",EDGE,{"derivedFrom":sQuery(id+"F16.wireOp",EDGE,"E87.MirrorCS")}),1.0]])]});
            var Q3;
            Q3=makeQuery(id+"F2.opExtrude","CAP_FACE",FACE,{"disambiguationData":[OSD([sQuery(id+"F0.wireOp",EDGE,"E12"),sQuery(id+"F0.wireOp",EDGE,"E13"),sQuery(id+"F0.wireOp",EDGE,"E14"),sQuery(id+"F0.wireOp",EDGE,"E15"),sQuery(id+"F0.wireOp",EDGE,"E17.filletArc"),sQuery(id+"F0.wireOp",EDGE,"E18.filletArc"),sQuery(id+"F0.wireOp",EDGE,"E19.filletArc"),sQuery(id+"F0.wireOp",EDGE,"E20.filletArc"),sQuery(id+"F0.wireOp",EDGE,"E25.0"),sQuery(id+"F0.wireOp",EDGE,"E25.1"),sQuery(id+"F0.wireOp",EDGE,"E25.2"),sQuery(id+"F0.wireOp",EDGE,"E25.3"),sQuery(id+"F0.wireOp",EDGE,"E25.4"),sQuery(id+"F0.wireOp",EDGE,"E25.5"),sQuery(id+"F0.wireOp",EDGE,"E25.6"),sQuery(id+"F0.wireOp",EDGE,"E25.7")])],"isStart":false});
            extrude(context, id + "F17", {"entities" : qUnion([Q0, Q1, Q2]), "endBound" : BoundingType.UP_TO_SURFACE, "endBoundEntityFace" : qUnion([Q3]), "depth" : 3 * mm});
        }
    });
